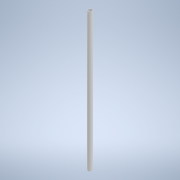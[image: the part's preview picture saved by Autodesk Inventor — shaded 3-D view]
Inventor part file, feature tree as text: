
AUTODESK INVENTOR PART (.ipt)
format: ipt  version: 2022 (Build 260153000, 153)  size: 169,984 bytes
history: native  units: mm
features: extrude x2, sketch x2
ambient origin geometry x8: Origin, YZ Plane, XZ Plane, XY Plane, X Axis, Y Axis, Z Axis, Center Point
bodies: Body1 (feature_tree)
feature tree (4):
  extrude  "Extrusion5"  Depth=15.0mm
  extrude  "Extrusion6"  Depth=5.0mm TaperAngle=0.0deg
  sketch  "Sketch2"  dims[d31=34.456mm d91=15.0mm]
  sketch  "Sketch3"  dims[d92=13.0mm d93=500.0mm d94=0.0mm d95=5.0mm d96=3.0mm d97=20.0mm d98=10.0mm d99=0.0mm d100=0.0mm d101=5.0mm d102=3.0mm]
